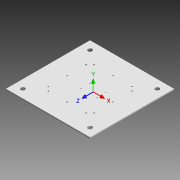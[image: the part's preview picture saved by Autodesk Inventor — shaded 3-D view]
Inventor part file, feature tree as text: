
AUTODESK INVENTOR PART (.ipt)
format: ipt  version: 2015 (Build 190159000, 159)  size: 243,712 bytes
history: native  units: in
note: dims shown in document units (in); Inventor stores cm internally (conversion verified against a paired STEP export)
features: reference x13, other x10, sketch x6, hole x3, sheet_metal_op x1
ambient origin geometry x8: Origin, YZ Plane, XZ Plane, XY Plane, X Axis, Y Axis, Z Axis, Center Point
bodies: Solid1 (feature_tree)
feature tree (33):
  sheet_metal_op  "Face1"
  other  "UCS1"
  hole  "Hole1"  [1 undecoded]
  hole  "Hole2"  [1 undecoded]
  sketch  "Sketch9"  dims[d40=0.75in]
  hole  "Hole3"  [1 undecoded]
  sketch  "Sketch1"  dims[d1=0.7874in d3=0.7874in d5=0.7874in d7=0.7874in d9=0.7874in d11=0.7874in d13=0.7874in d15=0.7874in d16=0.75in d17=0.75in d18=0.75in d19=0.75in d20=0.25in d21=0.25in d22=0.25in d23=0.25in d24=2.5681in d25=0.375in d26=1.5in d27=1.5in d28=1.5in d29=1.5in d30=1.5in d31=1.5in d32=1.5in d33=1.5in d34=90.0deg]
  other  "Plate1"
  sketch  "Sketch2"  dims[d35=45.0deg d36=90.0deg]
  sketch  "Sketch7"  dims[d37=90.0deg d38=90.0deg]
  sketch  "Sketch8"  dims[d39=0.125in]
  sketch  "Sketch10"  dims[d41=0.75in d42=5.313in d43=6.063in d44=11.376in d45=6.063in d46=0.25in d47=0.0in d48=4.2872in d49=5.9746in d50=6.063in d51=0.25in d52=8.3244in d53=4.2872in d54=0.125in d55=8.4494in d56=0.0625in d57=10.0in d58=10.0in d59=0.125in d60=8.0in d61=0.5in d62=0.5in d63=0.5in d64=0.5in d65=0.125in d66=0.0in d70=-2.5491in d71=0.0in d72=3.032in d73=0.0in d74=0.0in d75=0.0in d76=0.14in d77=0.75in d78=0.375in d79=0.25in d80=0.5635in d81=0.125in d82=0.8108in d83=0.144in d84=0.75in d85=0.279in d86=0.25in d87=0.5635in d88=0.125in d89=0.8108in d90=3.6662in d91=4.4695in d92=0.177in d93=0.328in d94=0.332in d95=0.25in d96=0.5635in d97=0.484in d98=0.8108in]
  reference  "Reference1"
  reference  "Reference2"
  reference  "Reference3"
  reference  "Reference4"
  reference  "Reference5"
  reference  "Reference6"
  reference  "Reference7"
  reference  "Reference8"
  reference  "Reference9"
  reference  "Reference10"
  reference  "Reference11"
  reference  "Reference12"
  reference  "Reference13"
  other  "Cut1"
  other  "UCS1: YZ Plane"
  other  "UCS1: XZ Plane"
  other  "UCS1: XY Plane"
  other  "UCS1: X Axis"
  other  "UCS1: Y Axis"
  other  "UCS1: Z Axis"
  other  "UCS1: Center Point"
note: 3 required parameter values undecoded (feature->parameter linkage not recoverable at this tier; creation-order binding heuristic only, values carry confidence <= 0.55)
